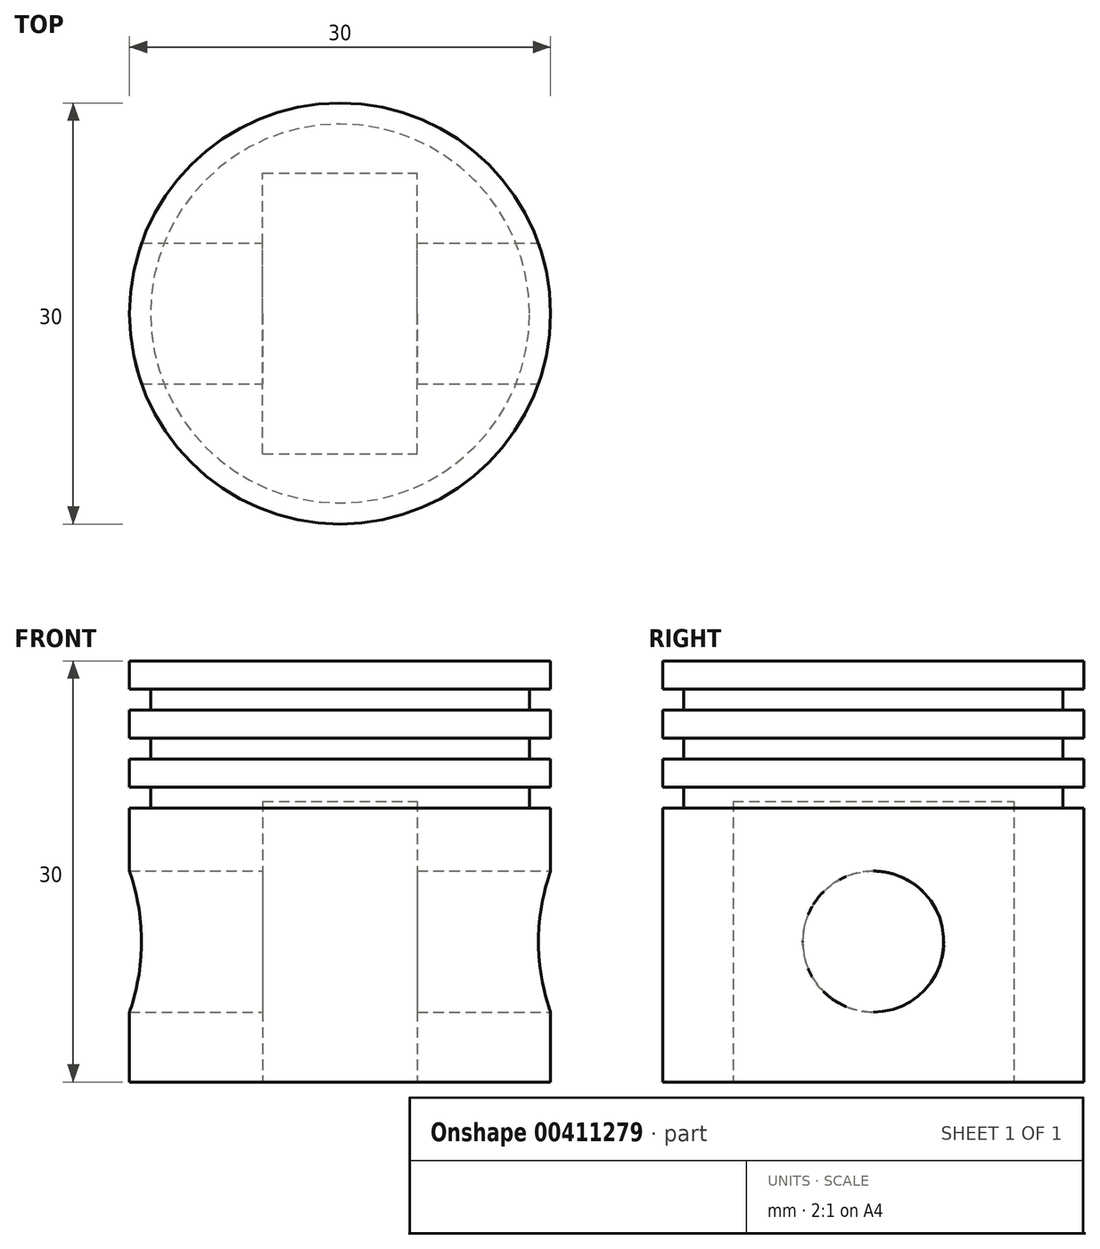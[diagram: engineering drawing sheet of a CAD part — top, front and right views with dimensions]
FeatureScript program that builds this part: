
annotation { "Feature Type Name" : "Feature", "Feature Type Description" : "" }
export const myFeature = defineFeature(function(context is Context, id is Id, definition is map)
    precondition{}
    {
        {
            var Q0;
            Q0=qCreatedBy(makeId("Front.planeOp"),FACE);
            var sketch = newSketch(context, id + "F0", { "sketchPlane" : qUnion([Q0])});
            skLineSegment(sketch, "E0.bottom", {"start": v(0, 15) * mm, "end": v(15, 15) * mm});
            skLineSegment(sketch, "E0.top", {"start": v(0, -15) * mm, "end": v(15, -15) * mm});
            skLineSegment(sketch, "E0.left", {"start": v(0, 15) * mm, "end": v(0, -15) * mm});
            skLineSegment(sketch, "E0.right", {"start": v(15, 15) * mm, "end": v(15, 13) * mm});
            skLineSegment(sketch, "E1.bottom", {"start": v(15, 13) * mm, "end": v(13.5, 13) * mm});
            skLineSegment(sketch, "E1.top", {"start": v(15, 11.5) * mm, "end": v(13.5, 11.5) * mm});
            skLineSegment(sketch, "E1.right", {"start": v(13.5, 13) * mm, "end": v(13.5, 11.5) * mm});
            skLineSegment(sketch, "E2.bottom", {"start": v(15, 9.5) * mm, "end": v(13.5, 9.5) * mm});
            skLineSegment(sketch, "E2.top", {"start": v(15, 8) * mm, "end": v(13.5, 8) * mm});
            skLineSegment(sketch, "E2.right", {"start": v(13.5, 9.5) * mm, "end": v(13.5, 8) * mm});
            skLineSegment(sketch, "E3.bottom", {"start": v(15, 6) * mm, "end": v(13.5, 6) * mm});
            skLineSegment(sketch, "E3.top", {"start": v(15, 4.5) * mm, "end": v(13.5, 4.5) * mm});
            skLineSegment(sketch, "E3.right", {"start": v(13.5, 6) * mm, "end": v(13.5, 4.5) * mm});
            skLineSegment(sketch, "E4.trimOffspring", {"start": v(15, 11.5) * mm, "end": v(15, 9.5) * mm});
            skLineSegment(sketch, "E5.trimOffspring", {"start": v(15, 8) * mm, "end": v(15, 6) * mm});
            skLineSegment(sketch, "E6.trimOffspring", {"start": v(15, 4.5) * mm, "end": v(15, -15) * mm});
            skLineSegment(sketch, "E7", {"start": v(0, 0) * mm, "end": v(15, 0) * mm, "construction": true});
            skSolve(sketch);
        }
        {
            var Q0;
            Q0 = qSketchRegion(id + "F0", true);
            var Q1;
            Q1=sQuery(id+"F0.wireOp",EDGE,"E0.left");
            revolve(context, id + "F1", {"entities" : qUnion([Q0]), "axis" : qUnion([Q1]), "revolveType" : RevolveType.FULL});
        }
        {
            var Q0;
            Q0=qCreatedBy(makeId("Right.planeOp"),FACE);
            var sketch = newSketch(context, id + "F2", { "sketchPlane" : qUnion([Q0])});
            skCircle(sketch, "E8", {"center": v(0, -5) * mm, "radius": 5.03 * mm});
            skSolve(sketch);
        }
        {
            var Q0;
            Q0 = qSketchRegion(id + "F2", true);
            extrude(context, id + "F3", {"entities" : qUnion([Q0]), "operationType" : NewBodyOperationType.REMOVE, "endBound" : BoundingType.SYMMETRIC, "oppositeDirection" : true, "depth" : 50 * mm});
        }
        {
            var Q0;
            Q0=makeQuery(id+"F1.opRevolve","SWEPT_FACE",FACE,{"disambiguationData":[OSD([sQuery(id+"F0.wireOp",EDGE,"E0.top")])]});
            var sketch = newSketch(context, id + "F4", { "sketchPlane" : qUnion([Q0])});
            skLineSegment(sketch, "E9.bottom", {"start": v(-5.5, 10) * mm, "end": v(5.5, 10) * mm});
            skLineSegment(sketch, "E9.top", {"start": v(-5.5, -10) * mm, "end": v(5.5, -10) * mm});
            skLineSegment(sketch, "E9.left", {"start": v(-5.5, 10) * mm, "end": v(-5.5, -10) * mm});
            skLineSegment(sketch, "E9.right", {"start": v(5.5, 10) * mm, "end": v(5.5, -10) * mm});
            skPoint(sketch, "E9.middle", {"position": v(0, 0) * mm});
            skSolve(sketch);
        }
        {
            var Q0;
            Q0 = qSketchRegion(id + "F4", true);
            extrude(context, id + "F5", {"entities" : qUnion([Q0]), "operationType" : NewBodyOperationType.REMOVE, "oppositeDirection" : true, "depth" : 20 * mm});
        }
    });
